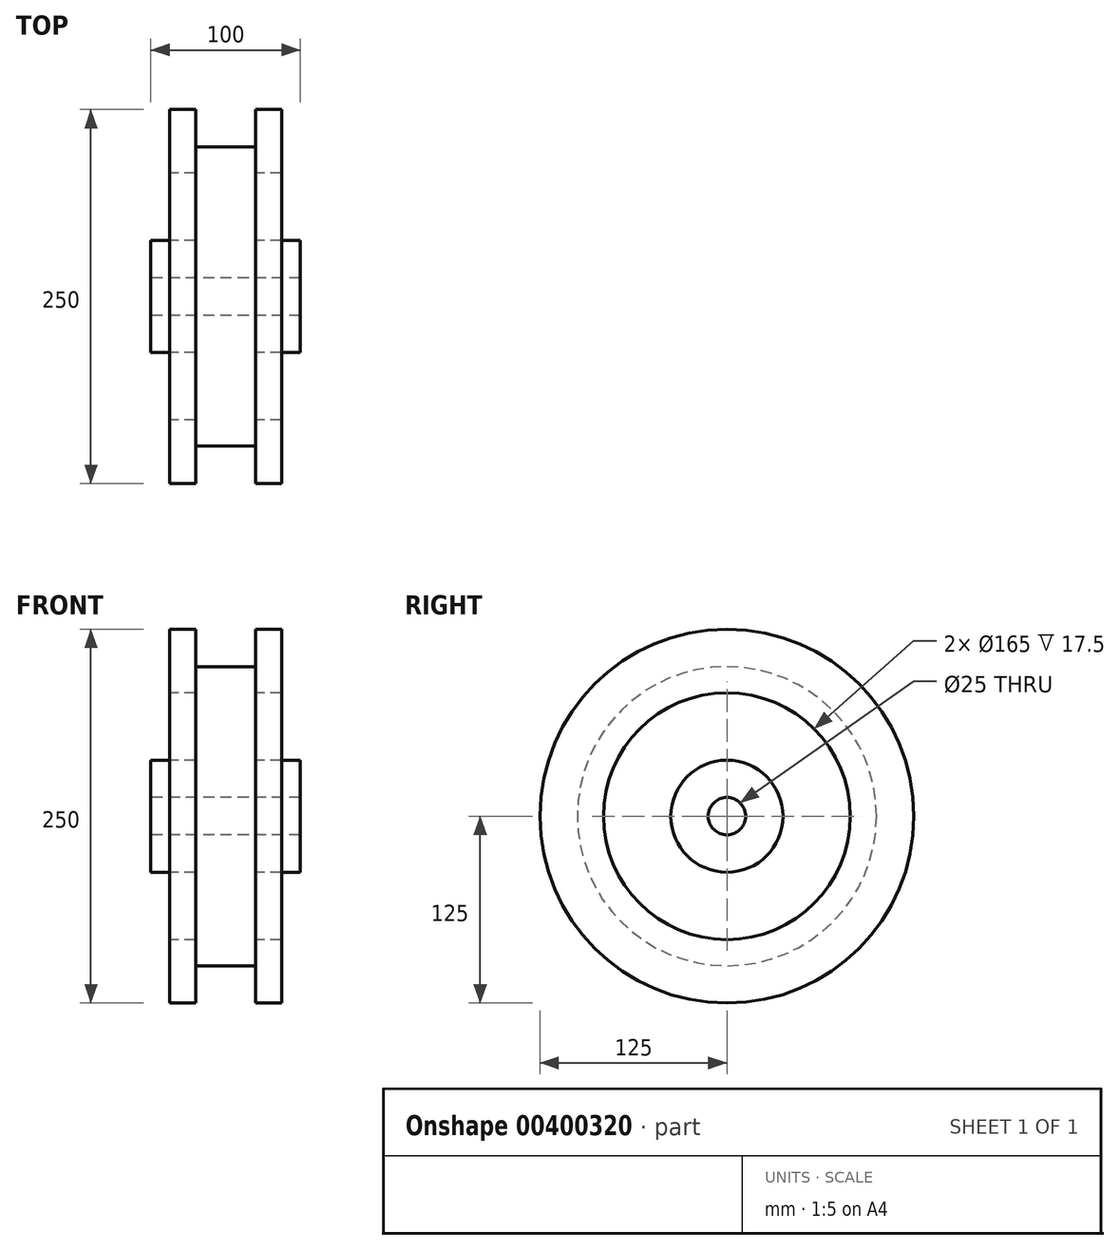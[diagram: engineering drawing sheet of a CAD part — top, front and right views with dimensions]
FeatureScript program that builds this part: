
annotation { "Feature Type Name" : "Feature", "Feature Type Description" : "" }
export const myFeature = defineFeature(function(context is Context, id is Id, definition is map)
    precondition{}
    {
        {
            var Q0;
            Q0=qCreatedBy(makeId("Front.planeOp"),FACE);
            var sketch = newSketch(context, id + "F0", { "sketchPlane" : qUnion([Q0])});
            skLineSegment(sketch, "E0", {"start": v(0, 0) * mm, "end": v(112.81, 0) * mm, "construction": true});
            skLineSegment(sketch, "E1", {"start": v(0, 0) * mm, "end": v(0, 121.5) * mm, "construction": true});
            skLineSegment(sketch, "E2", {"start": v(0, 12.5) * mm, "end": v(-50, 12.5) * mm});
            skLineSegment(sketch, "E3", {"start": v(-50, 12.5) * mm, "end": v(-50, 37.5) * mm});
            skLineSegment(sketch, "E4", {"start": v(-37.5, 125) * mm, "end": v(-20, 125) * mm});
            skLineSegment(sketch, "E5", {"start": v(-20, 125) * mm, "end": v(-20, 100) * mm});
            skLineSegment(sketch, "E6", {"start": v(-20, 100) * mm, "end": v(0, 100) * mm});
            skLineSegment(sketch, "E7", {"start": v(-50, 37.5) * mm, "end": v(-20, 37.5) * mm});
            skLineSegment(sketch, "E8", {"start": v(-20, 37.5) * mm, "end": v(-20, 82.5) * mm});
            skLineSegment(sketch, "E9", {"start": v(-20, 82.5) * mm, "end": v(-37.5, 82.5) * mm});
            skLineSegment(sketch, "E10.trimOffspring", {"start": v(-37.5, 82.5) * mm, "end": v(-37.5, 125) * mm});
            skLineSegment(sketch, "E11.MirrorCS", {"start": v(37.5, 125) * mm, "end": v(20, 125) * mm});
            skLineSegment(sketch, "E12.MirrorCS", {"start": v(37.5, 82.5) * mm, "end": v(37.5, 125) * mm});
            skLineSegment(sketch, "E13.MirrorCS", {"start": v(50, 37.5) * mm, "end": v(20, 37.5) * mm});
            skLineSegment(sketch, "E14.MirrorCS", {"start": v(20, 82.5) * mm, "end": v(37.5, 82.5) * mm});
            skLineSegment(sketch, "E15.MirrorCS", {"start": v(20, 100) * mm, "end": v(0, 100) * mm});
            skLineSegment(sketch, "E16.MirrorCS", {"start": v(20, 37.5) * mm, "end": v(20, 82.5) * mm});
            skLineSegment(sketch, "E17.MirrorCS", {"start": v(0, 12.5) * mm, "end": v(50, 12.5) * mm});
            skLineSegment(sketch, "E18.MirrorCS", {"start": v(20, 125) * mm, "end": v(20, 100) * mm});
            skLineSegment(sketch, "E19.MirrorCS", {"start": v(50, 12.5) * mm, "end": v(50, 37.5) * mm});
            skSolve(sketch);
        }
        {
            var Q0;
            Q0 = qSketchRegion(id + "F0", true);
            var Q1;
            Q1=sQuery(id+"F0.wireOp",EDGE,"E0");
            revolve(context, id + "F1", {"surfaceOperationType" : NewSurfaceOperationType.NEW, "entities" : qUnion([Q0]), "axis" : qUnion([Q1]), "revolveType" : RevolveType.FULL});
        }
    });
